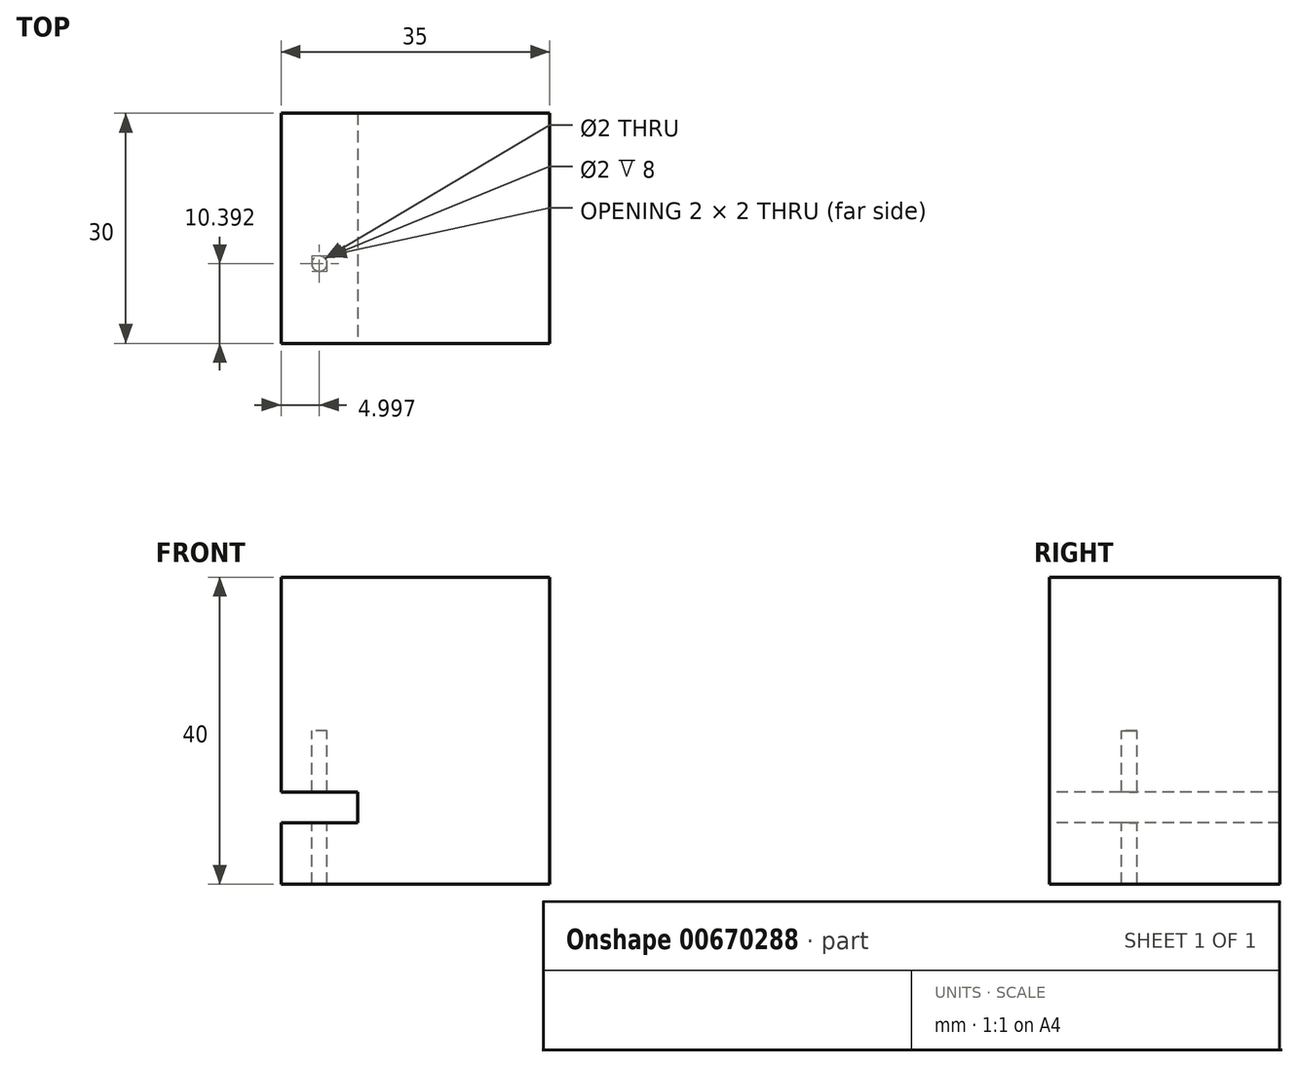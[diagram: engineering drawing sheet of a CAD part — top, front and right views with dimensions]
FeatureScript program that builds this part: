
annotation { "Feature Type Name" : "Feature", "Feature Type Description" : "" }
export const myFeature = defineFeature(function(context is Context, id is Id, definition is map)
    precondition{}
    {
        {
            var Q0;
            Q0=qCreatedBy(makeId("Top.planeOp"),FACE);
            var sketch = newSketch(context, id + "F0", { "sketchPlane" : qUnion([Q0])});
            skLineSegment(sketch, "E0.bottom", {"start": v(-23.24, -27.36) * mm, "end": v(11.76, -27.36) * mm});
            skLineSegment(sketch, "E0.top", {"start": v(-23.24, 2.64) * mm, "end": v(11.76, 2.64) * mm});
            skLineSegment(sketch, "E0.left", {"start": v(-23.24, -27.36) * mm, "end": v(-23.24, 2.64) * mm});
            skLineSegment(sketch, "E0.right", {"start": v(11.76, -27.36) * mm, "end": v(11.76, 2.64) * mm});
            skSolve(sketch);
        }
        {
            var Q0;
            Q0=makeQuery(id+"F0.imprint","IMPRINT",FACE,{"disambiguationData":[TD([[makeQuery(id+"F0.imprint","IMPRINT",EDGE,{"derivedFrom":sQuery(id+"F0.wireOp",EDGE,"E0.bottom")}),1.0]])]});
            extrude(context, id + "F1", {"entities" : qUnion([Q0]), "depth" : 20 * mm, "offsetDistance" : 25 * mm});
        }
        {
            var Q0;
            Q0=makeQuery(id+"F1.opExtrude","SWEPT_FACE",FACE,{"disambiguationData":[OSD([sQuery(id+"F0.wireOp",EDGE,"E0.bottom")])]});
            var sketch = newSketch(context, id + "F2", { "sketchPlane" : qUnion([Q0])});
            skLineSegment(sketch, "E1.top", {"start": v(-23.24, 12) * mm, "end": v(-13.24, 12) * mm});
            skLineSegment(sketch, "E2.top", {"start": v(-23.24, 8) * mm, "end": v(-13.24, 8) * mm});
            skLineSegment(sketch, "E2.left", {"start": v(-23.24, 12) * mm, "end": v(-23.24, 8) * mm});
            skLineSegment(sketch, "E2.right", {"start": v(-13.24, 12) * mm, "end": v(-13.24, 8) * mm});
            skSolve(sketch);
        }
        {
            var Q0;
            Q0 = qSketchRegion(id + "F2", true);
            extrude(context, id + "F3", {"entities" : qUnion([Q0]), "operationType" : NewBodyOperationType.REMOVE, "oppositeDirection" : true, "depth" : 40 * mm, "offsetDistance" : 25 * mm});
        }
        {
            var Q0;
            Q0=makeQuery(id+"F1.opExtrude","CAP_FACE",FACE,{"disambiguationData":[OSD([sQuery(id+"F0.wireOp",EDGE,"E0.bottom"),sQuery(id+"F0.wireOp",EDGE,"E0.top"),sQuery(id+"F0.wireOp",EDGE,"E0.left"),sQuery(id+"F0.wireOp",EDGE,"E0.right")])],"isStart":false});
            var sketch = newSketch(context, id + "F4", { "sketchPlane" : qUnion([Q0])});
            skCircle(sketch, "E3", {"center": v(-18.24, 3.9) * mm, "radius": 1 * mm});
            skCircle(sketch, "E4", {"center": v(-18.24, -16.97) * mm, "radius": 1 * mm});
            skSolve(sketch);
        }
        {
            var Q0;
            Q0 = qSketchRegion(id + "F4", true);
            extrude(context, id + "F5", {"entities" : qUnion([Q0]), "operationType" : NewBodyOperationType.REMOVE, "oppositeDirection" : true, "depth" : 25 * mm, "offsetDistance" : 25 * mm});
        }
        {
            var Q0;
            Q0=makeQuery(id+"F1.opExtrude","CAP_FACE",FACE,{"disambiguationData":[OSD([sQuery(id+"F0.wireOp",EDGE,"E0.bottom"),sQuery(id+"F0.wireOp",EDGE,"E0.top"),sQuery(id+"F0.wireOp",EDGE,"E0.left"),sQuery(id+"F0.wireOp",EDGE,"E0.right")])],"isStart":false});
            var sketch = newSketch(context, id + "F6", { "sketchPlane" : qUnion([Q0])});
            skLineSegment(sketch, "E5.bottom", {"start": v(-21.27, -35) * mm, "end": v(-23.24, -35) * mm});
            skLineSegment(sketch, "E5.top", {"start": v(-21.27, -3.7) * mm, "end": v(-23.24, -3.7) * mm});
            skLineSegment(sketch, "E5.left", {"start": v(-21.27, -35) * mm, "end": v(-21.27, -3.7) * mm});
            skLineSegment(sketch, "E6.bottom", {"start": v(-23.24, 2.64) * mm, "end": v(11.76, 2.64) * mm});
            skLineSegment(sketch, "E6.top", {"start": v(-23.24, -27.36) * mm, "end": v(11.76, -27.36) * mm});
            skLineSegment(sketch, "E6.left", {"start": v(-23.24, 2.64) * mm, "end": v(-23.24, -27.36) * mm});
            skLineSegment(sketch, "E6.right", {"start": v(11.76, 2.64) * mm, "end": v(11.76, -27.36) * mm});
            skSolve(sketch);
        }
        {
            var Q0;
            Q0 = qSketchRegion(id + "F6", true);
            extrude(context, id + "F7", {"entities" : qUnion([Q0]), "operationType" : NewBodyOperationType.ADD, "depth" : 20 * mm, "offsetDistance" : 25 * mm});
        }
    });
